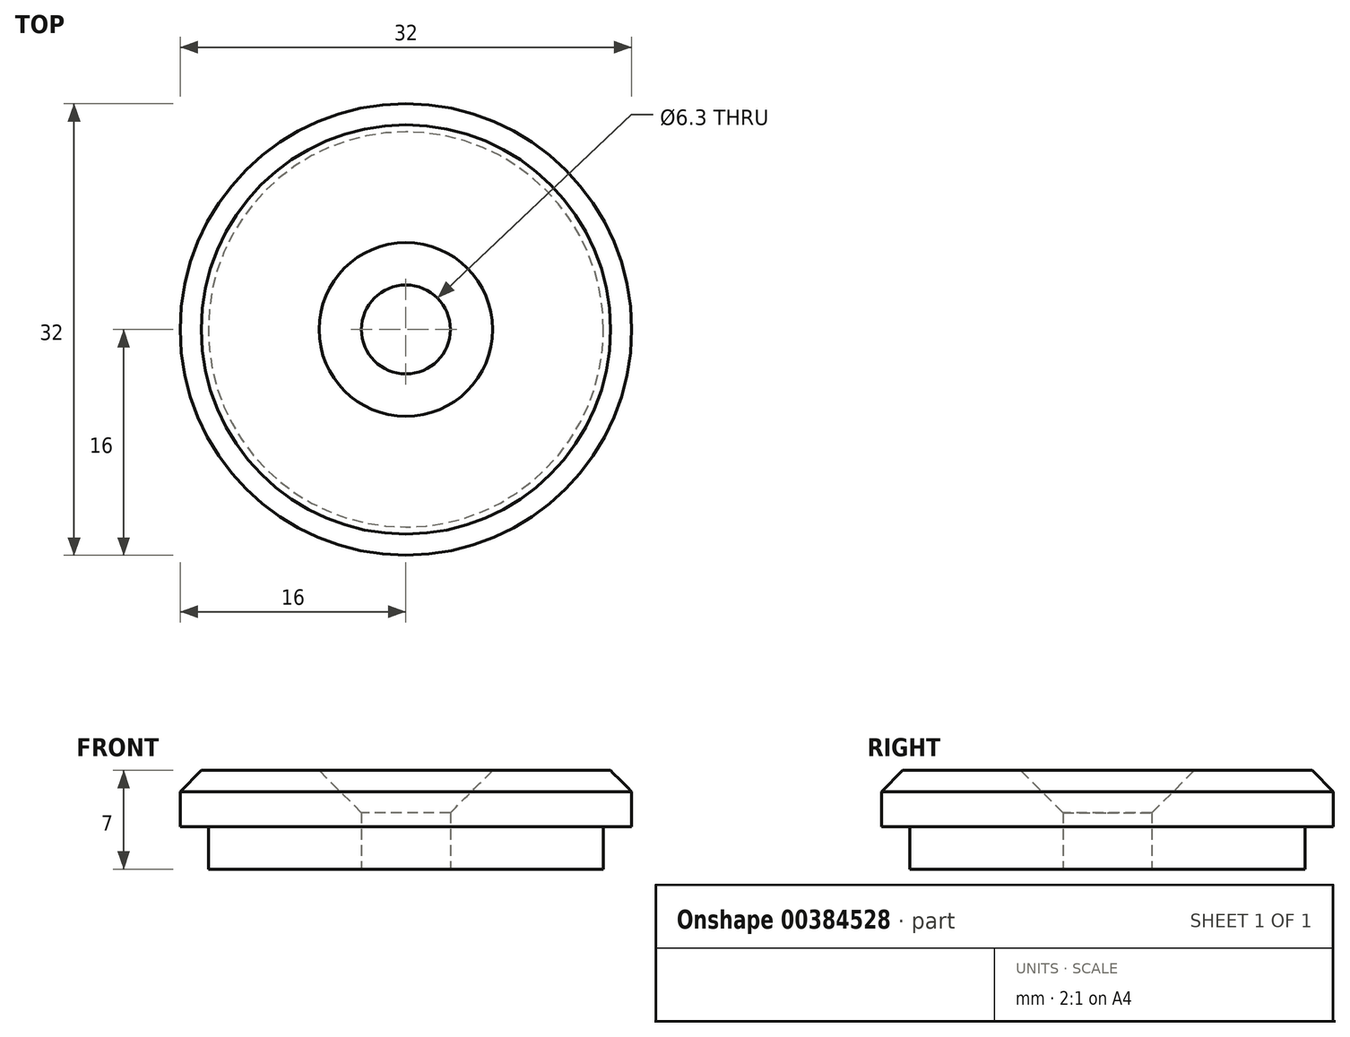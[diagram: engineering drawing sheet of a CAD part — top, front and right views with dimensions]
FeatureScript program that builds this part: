
annotation { "Feature Type Name" : "Feature", "Feature Type Description" : "" }
export const myFeature = defineFeature(function(context is Context, id is Id, definition is map)
    precondition{}
    {
        {
            var Q0;
            Q0=qCreatedBy(makeId("Top.planeOp"),FACE);
            var sketch = newSketch(context, id + "F0", { "sketchPlane" : qUnion([Q0])});
            skCircle(sketch, "E0", {"center": v(0, 0) * mm, "radius": 16 * mm});
            skCircle(sketch, "E1", {"center": v(0, 0) * mm, "radius": 3.15 * mm});
            skCircle(sketch, "E2", {"center": v(0, 0) * mm, "radius": 14 * mm});
            skSolve(sketch);
        }
        {
            var Q0;
            Q0=makeQuery(id+"F0.imprint","IMPRINT",FACE,{"disambiguationData":[TD([[makeQuery(id+"F0.imprint","IMPRINT",EDGE,{"derivedFrom":sQuery(id+"F0.wireOp",EDGE,"E0")}),1.0]])]});
            var Q1;
            Q1=makeQuery(id+"F0.imprint","IMPRINT",FACE,{"disambiguationData":[TD([[makeQuery(id+"F0.imprint","IMPRINT",EDGE,{"derivedFrom":sQuery(id+"F0.wireOp",EDGE,"E1")}),-1.0]])]});
            extrude(context, id + "F1", {"entities" : qUnion([Q0, Q1]), "depth" : 4 * mm});
        }
        {
            var Q0;
            Q0=makeQuery(id+"F0.imprint","IMPRINT",FACE,{"disambiguationData":[TD([[makeQuery(id+"F0.imprint","IMPRINT",EDGE,{"derivedFrom":sQuery(id+"F0.wireOp",EDGE,"E1")}),-1.0]])]});
            extrude(context, id + "F2", {"entities" : qUnion([Q0]), "operationType" : NewBodyOperationType.ADD, "oppositeDirection" : true, "depth" : 3 * mm});
        }
        {
            var Q0;
            Q0=makeQuery(id+"F1.opExtrude","CAP_EDGE",EDGE,{"disambiguationData":[OSD([sQuery(id+"F0.wireOp",EDGE,"E1")])],"isStart":false});
            chamfer(context, id + "F3", {"entities" : qUnion([Q0]), "width" : 3 * mm, "tangentPropagation" : true});
        }
        {
            var Q0;
            Q0=makeQuery(id+"F1.opExtrude","CAP_EDGE",EDGE,{"disambiguationData":[OSD([sQuery(id+"F0.wireOp",EDGE,"E0")])],"isStart":false});
            chamfer(context, id + "F4", {"entities" : qUnion([Q0]), "width" : 1.5 * mm, "tangentPropagation" : true});
        }
    });
